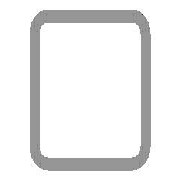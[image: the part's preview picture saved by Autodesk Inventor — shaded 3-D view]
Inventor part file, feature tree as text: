
AUTODESK INVENTOR PART (.ipt)
format: ipt  version: 2025.1 (Build 291241020, 241B)  size: 144,384 bytes
history: native  units: mm (DEFAULTED — no unit token found)
features: other x4, sketch x1, plane x1
ambient origin geometry x8: Origin, YZ Plane, XZ Plane, XY Plane, X Axis, Y Axis, Z Axis, Center Point
bodies: Solid1 (feature_tree), Body (feature_tree)
feature tree (6):
  parser-record x1  (decoder bookkeeping rows leaked as tree rows — omitted from the tree; the rows remain in map.json)
  other  "Driven Length"
  other  "Start plane"
  other  "End plane"
  sketch  "Sketch3"  dims[d3=950.0mm d4=0.0mm d7=6.0mm d9=100.0mm d11=100.0mm d12=3.0mm d13=50.0mm d14=1000.0mm d15=50.0mm d16=50.0mm d17=90.0deg d18=950.0mm]
  plane  "Work Plane3"
